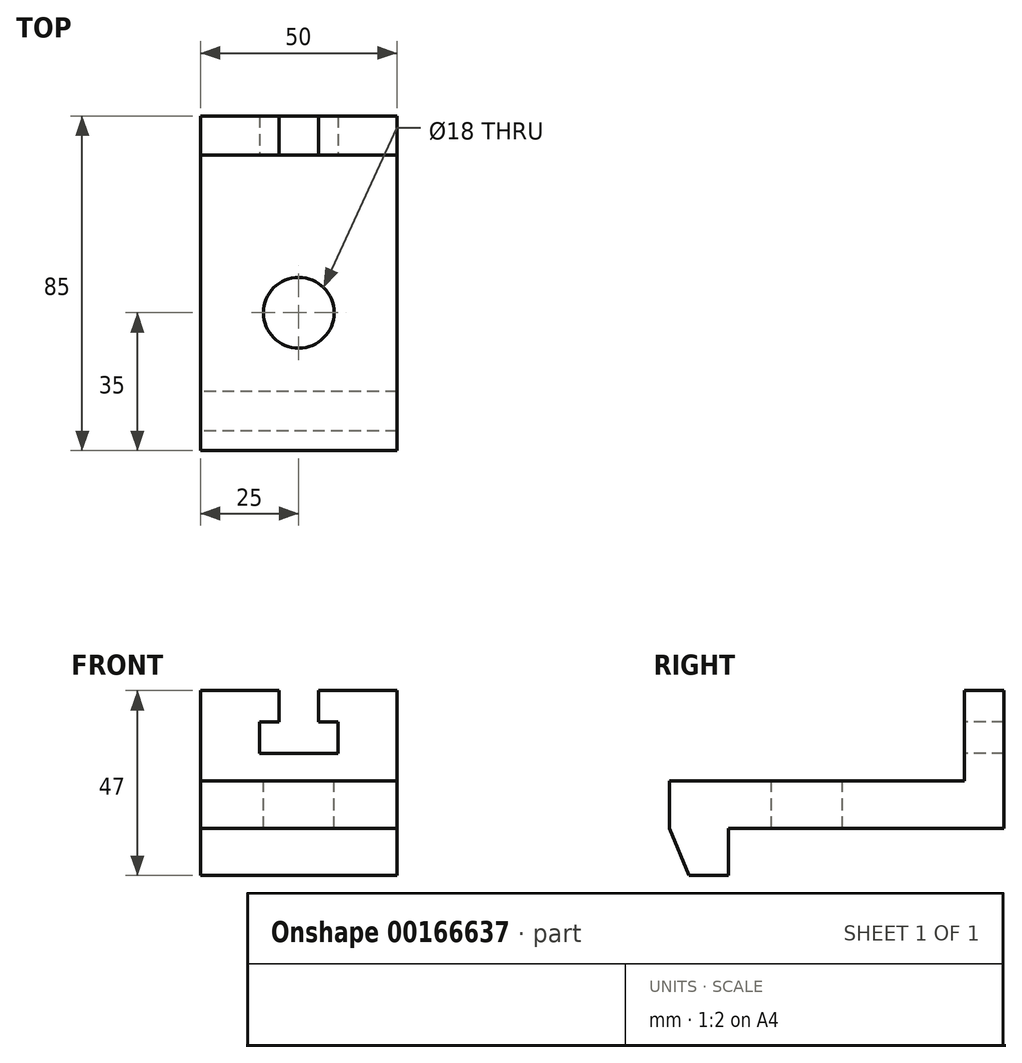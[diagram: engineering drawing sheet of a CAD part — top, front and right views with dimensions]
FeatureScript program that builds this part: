
annotation { "Feature Type Name" : "Feature", "Feature Type Description" : "" }
export const myFeature = defineFeature(function(context is Context, id is Id, definition is map)
    precondition{}
    {
        {
            var Q0;
            Q0=qCreatedBy(makeId("Right.planeOp"),FACE);
            var sketch = newSketch(context, id + "F0", { "sketchPlane" : qUnion([Q0])});
            skPoint(sketch, "E0.middle", {"position": v(0, 0) * mm});
            skLineSegment(sketch, "E1.bottom", {"start": v(37.5, 6) * mm, "end": v(-37.5, 6) * mm});
            skLineSegment(sketch, "E1.top", {"start": v(37.5, -6) * mm, "end": v(-37.5, -6) * mm});
            skLineSegment(sketch, "E1.left", {"start": v(37.5, 6) * mm, "end": v(37.5, -6) * mm});
            skLineSegment(sketch, "E1.right", {"start": v(-37.5, 6) * mm, "end": v(-37.5, -6) * mm});
            skLineSegment(sketch, "E2", {"start": v(37.5, -6) * mm, "end": v(37.5, 29) * mm});
            skLineSegment(sketch, "E3", {"start": v(37.5, -6) * mm, "end": v(47.5, -6) * mm});
            skLineSegment(sketch, "E4", {"start": v(47.5, -6) * mm, "end": v(47.5, 29) * mm});
            skLineSegment(sketch, "E5", {"start": v(47.5, 29) * mm, "end": v(37.5, 29) * mm});
            skLineSegment(sketch, "E6.bottom", {"start": v(-37.5, -6) * mm, "end": v(-22.5, -6) * mm});
            skLineSegment(sketch, "E6.right", {"start": v(-22.5, -6) * mm, "end": v(-22.5, -18) * mm});
            skLineSegment(sketch, "E7", {"start": v(-22.5, -18) * mm, "end": v(-32.5, -18) * mm});
            skLineSegment(sketch, "E8", {"start": v(-37.5, -6) * mm, "end": v(-32.5, -18) * mm});
            skSolve(sketch);
        }
        {
            var Q0;
            Q0 = qSketchRegion(id + "F0", true);
            extrude(context, id + "F1", {"entities" : qUnion([Q0]), "depth" : 50 * mm});
        }
        {
            var Q0;
            Q0=makeQuery(id+"F1.opExtrude","SWEPT_FACE",FACE,{"disambiguationData":[OSD([sQuery(id+"F0.wireOp",EDGE,"E2")])]});
            var sketch = newSketch(context, id + "F2", { "sketchPlane" : qUnion([Q0])});
            skLineSegment(sketch, "E9", {"start": v(50, 29) * mm, "end": v(30, 29) * mm});
            skLineSegment(sketch, "E10", {"start": v(0, 29) * mm, "end": v(20, 29) * mm});
            skLineSegment(sketch, "E11", {"start": v(20, 29) * mm, "end": v(20, 21) * mm});
            skLineSegment(sketch, "E12", {"start": v(30, 29) * mm, "end": v(30, 21) * mm});
            skLineSegment(sketch, "E13", {"start": v(20, 21) * mm, "end": v(15, 21) * mm});
            skLineSegment(sketch, "E14", {"start": v(30, 21) * mm, "end": v(35, 21) * mm});
            skLineSegment(sketch, "E15", {"start": v(15, 21) * mm, "end": v(15, 13) * mm});
            skLineSegment(sketch, "E16", {"start": v(35, 21) * mm, "end": v(35, 13) * mm});
            skLineSegment(sketch, "E17", {"start": v(35, 13) * mm, "end": v(15, 13) * mm});
            skLineSegment(sketch, "E18", {"start": v(30, 29) * mm, "end": v(20, 29) * mm});
            skSolve(sketch);
        }
        {
            var Q0;
            Q0 = qSketchRegion(id + "F2", true);
            extrude(context, id + "F3", {"entities" : qUnion([Q0]), "operationType" : NewBodyOperationType.REMOVE, "oppositeDirection" : true, "depth" : 25 * mm});
        }
        {
            var Q0;
            Q0=makeQuery(id+"F1.opExtrude","SWEPT_FACE",FACE,{"disambiguationData":[OSD([sQuery(id+"F0.wireOp",EDGE,"E1.bottom")])]});
            var sketch = newSketch(context, id + "F4", { "sketchPlane" : qUnion([Q0])});
            skCircle(sketch, "E19", {"center": v(25, -2.5) * mm, "radius": 9 * mm});
            skSolve(sketch);
        }
        {
            var Q0;
            Q0 = qSketchRegion(id + "F4", true);
            extrude(context, id + "F5", {"entities" : qUnion([Q0]), "operationType" : NewBodyOperationType.REMOVE, "oppositeDirection" : true, "depth" : 25 * mm});
        }
    });
